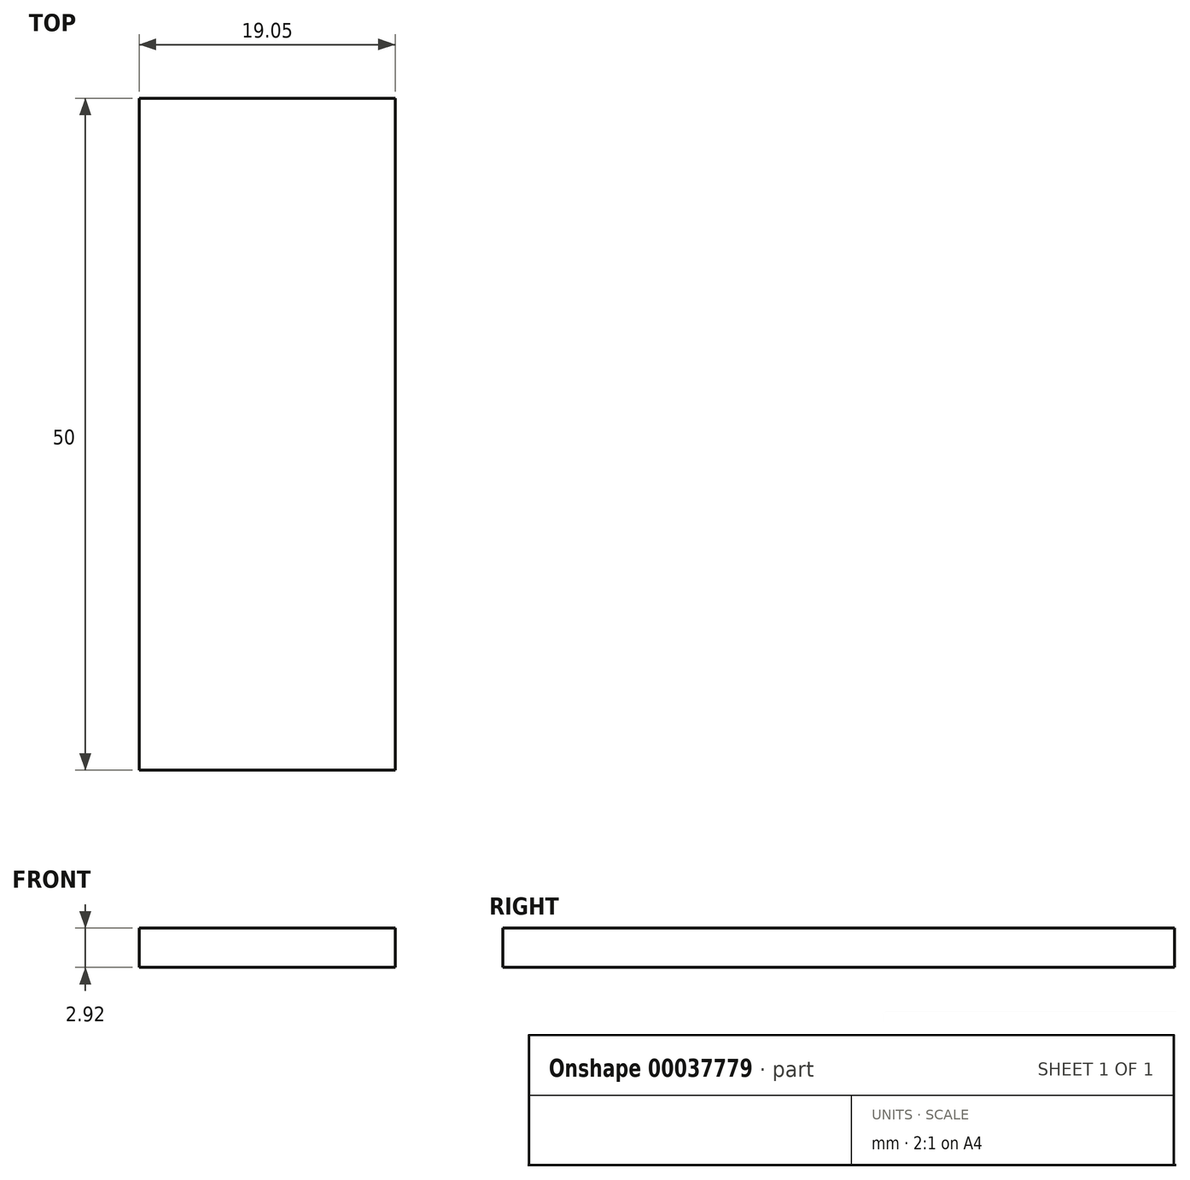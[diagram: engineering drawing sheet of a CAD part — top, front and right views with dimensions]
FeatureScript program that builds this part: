
annotation { "Feature Type Name" : "Feature", "Feature Type Description" : "" }
export const myFeature = defineFeature(function(context is Context, id is Id, definition is map)
    precondition{}
    {
        {
            var Q0;
            Q0=qCreatedBy(makeId("Top.planeOp"),FACE);
            var sketch = newSketch(context, id + "F0", { "sketchPlane" : qUnion([Q0])});
            skLineSegment(sketch, "E0.bottom", {"start": v(0, 0) * mm, "end": v(19.05, 0) * mm});
            skLineSegment(sketch, "E0.top", {"start": v(0, -50) * mm, "end": v(19.05, -50) * mm});
            skLineSegment(sketch, "E0.left", {"start": v(0, 0) * mm, "end": v(0, -50) * mm});
            skLineSegment(sketch, "E0.right", {"start": v(19.05, 0) * mm, "end": v(19.05, -50) * mm});
            skSolve(sketch);
        }
        {
            var Q0;
            Q0 = qSketchRegion(id + "F0", true);
            extrude(context, id + "F1", {"entities" : qUnion([Q0]), "depth" : 2.92 * mm});
        }
    });
